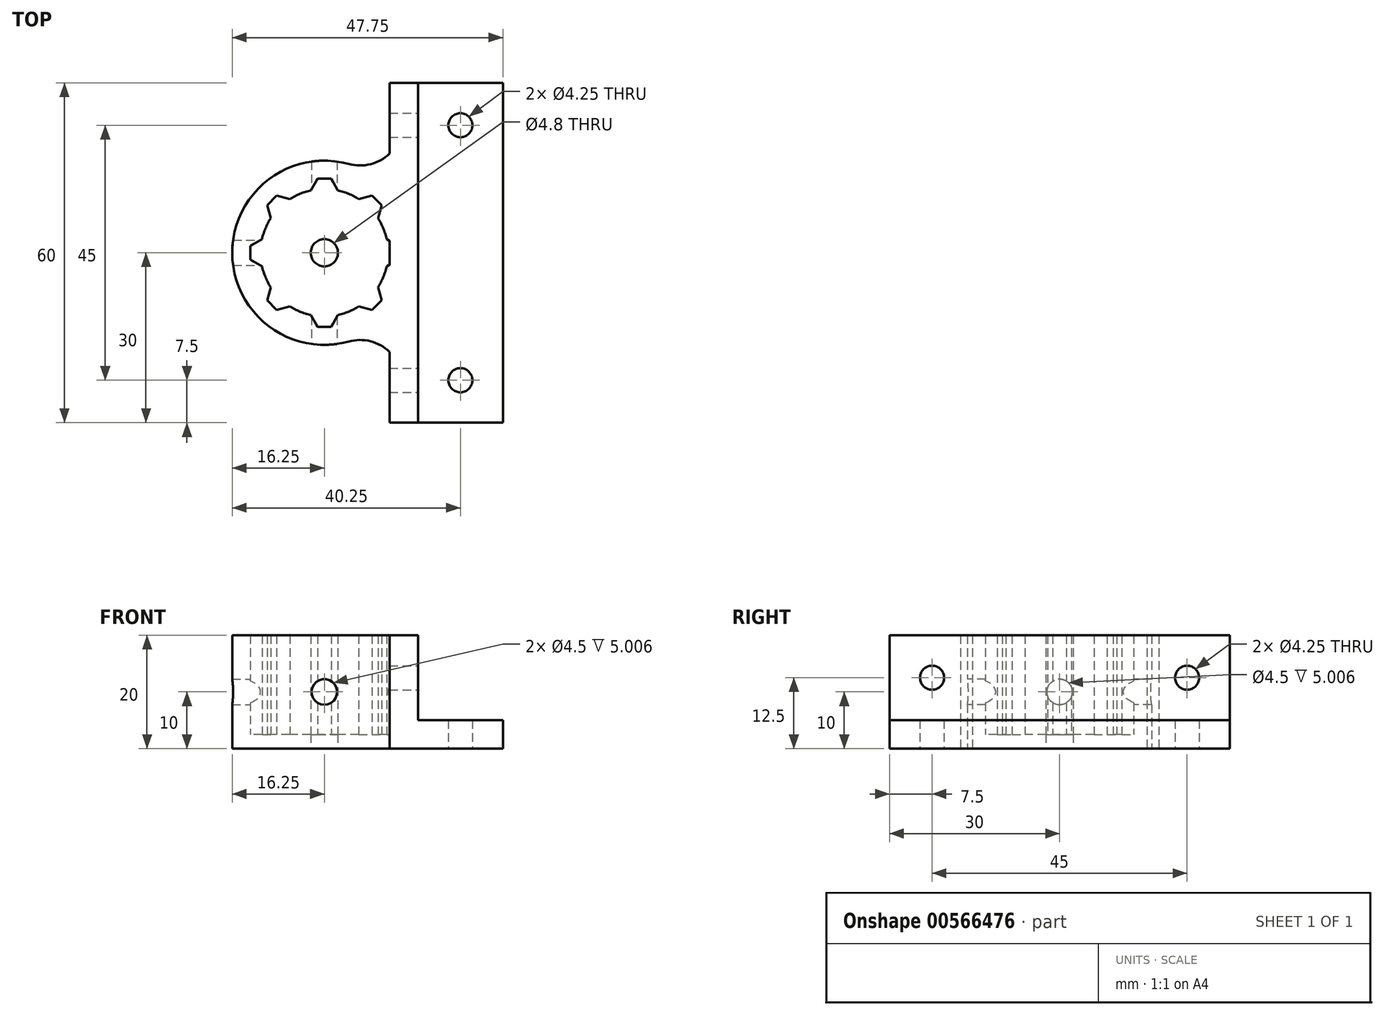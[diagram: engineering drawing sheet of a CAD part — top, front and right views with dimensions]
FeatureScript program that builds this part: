
annotation { "Feature Type Name" : "Feature", "Feature Type Description" : "" }
export const myFeature = defineFeature(function(context is Context, id is Id, definition is map)
    precondition{}
    {
        {
            var Q0;
            Q0=qCreatedBy(makeId("Top.planeOp"),FACE);
            var sketch = newSketch(context, id + "F0", { "sketchPlane" : qUnion([Q0])});
            skCircle(sketch, "E0", {"center": v(0, 0) * mm, "radius": 11 * mm, "construction": true});
            skLineSegment(sketch, "E1.bottom", {"start": v(7.5, -30) * mm, "end": v(-7.5, -30) * mm});
            skLineSegment(sketch, "E1.top", {"start": v(7.5, 30) * mm, "end": v(-7.5, 30) * mm});
            skLineSegment(sketch, "E1.left", {"start": v(7.5, -30) * mm, "end": v(7.5, 30) * mm});
            skLineSegment(sketch, "E1.right", {"start": v(-7.5, -30) * mm, "end": v(-7.5, 30) * mm});
            skCircle(sketch, "E2", {"center": v(0, 22.5) * mm, "radius": 2.12 * mm});
            skCircle(sketch, "E3.MirrorC", {"center": v(0, -22.5) * mm, "radius": 2.12 * mm});
            skSolve(sketch);
        }
        {
            var Q0;
            Q0=qSketchRegion(id+"F0",true);
            extrude(context, id + "F1", {"entities" : qUnion([Q0]), "depth" : 5 * mm});
        }
        {
            var Q0;
            Q0=makeQuery(id+"F1.opExtrude","SWEPT_FACE",FACE,{"disambiguationData":[OSD([sQuery(id+"F0.wireOp",EDGE,"E1.right")])]});
            var sketch = newSketch(context, id + "F2", { "sketchPlane" : qUnion([Q0])});
            skLineSegment(sketch, "E4.bottom", {"start": v(30, 0) * mm, "end": v(-30, 0) * mm});
            skLineSegment(sketch, "E4.top", {"start": v(30, 20) * mm, "end": v(-30, 20) * mm});
            skLineSegment(sketch, "E4.left", {"start": v(30, 0) * mm, "end": v(30, 20) * mm});
            skLineSegment(sketch, "E4.right", {"start": v(-30, 0) * mm, "end": v(-30, 20) * mm});
            skPoint(sketch, "E4.middle", {"position": v(0, 10) * mm});
            skCircle(sketch, "E5", {"center": v(-22.5, 12.5) * mm, "radius": 2.12 * mm});
            skCircle(sketch, "E6.MirrorC", {"center": v(22.5, 12.5) * mm, "radius": 2.12 * mm});
            skSolve(sketch);
        }
        {
            var Q0;
            Q0=qSketchRegion(id+"F2",true);
            extrude(context, id + "F3", {"entities" : qUnion([Q0]), "operationType" : NewBodyOperationType.ADD, "depth" : 5 * mm});
        }
        {
            var Q0;
            Q0=qCreatedBy(makeId("Top.planeOp"),FACE);
            var sketch = newSketch(context, id + "F4", { "sketchPlane" : qUnion([Q0])});
            skArc(sketch, "E7", {"start": v(-26.4, 11) * mm, "mid": v(-28.3, 10.4) * mm, "end": v(-30.07, 9.47) * mm});
            skArc(sketch, "E8", {"start": v(-19.7, 15.67) * mm, "mid": v(-40.25, 0) * mm, "end": v(-19.7, -15.67) * mm});
            skArc(sketch, "E9", {"start": v(-19.7, 15.67) * mm, "mid": v(-15.85, 15.63) * mm, "end": v(-12.5, 17.5) * mm});
            skArc(sketch, "E10.MirrorCS", {"start": v(-19.7, -15.67) * mm, "mid": v(-15.85, -15.63) * mm, "end": v(-12.5, -17.5) * mm});
            skLineSegment(sketch, "E11", {"start": v(-12.5, 17.5) * mm, "end": v(-12.5, 2.1) * mm});
            skCircle(sketch, "E12.cCircle", {"center": v(-13, 0) * mm, "radius": 2.08 * mm, "construction": true});
            skLineSegment(sketch, "E12.0", {"start": v(-10.93, 1.2) * mm, "end": v(-10.93, -1.2) * mm, "construction": true});
            skLineSegment(sketch, "E12.1", {"start": v(-12.5, -2.1) * mm, "end": v(-13, -2.4) * mm});
            skLineSegment(sketch, "E12.2", {"start": v(-13, -2.4) * mm, "end": v(-15.09, -1.2) * mm, "construction": true});
            skLineSegment(sketch, "E12.3", {"start": v(-15.09, -1.2) * mm, "end": v(-15.09, 1.2) * mm, "construction": true});
            skLineSegment(sketch, "E12.4", {"start": v(-15.09, 1.2) * mm, "end": v(-13, 2.4) * mm, "construction": true});
            skLineSegment(sketch, "E12.5", {"start": v(-13, 2.4) * mm, "end": v(-12.5, 2.1) * mm});
            skPoint(sketch, "E12.0.midPoint", {"position": v(-10.93, 0) * mm});
            skLineSegment(sketch, "E13.1.0", {"start": v(-17.93, 9.47) * mm, "end": v(-15.6, 10.1) * mm});
            skLineSegment(sketch, "E13.1.1", {"start": v(-15.6, 10.1) * mm, "end": v(-13.9, 8.4) * mm});
            skLineSegment(sketch, "E13.1.2", {"start": v(-13.9, 8.4) * mm, "end": v(-14.53, 6.07) * mm});
            skLineSegment(sketch, "E13.2.0", {"start": v(-26.4, 11) * mm, "end": v(-25.2, 13.07) * mm});
            skLineSegment(sketch, "E13.2.1", {"start": v(-25.2, 13.07) * mm, "end": v(-22.8, 13.07) * mm});
            skLineSegment(sketch, "E13.2.2", {"start": v(-22.8, 13.07) * mm, "end": v(-21.6, 11) * mm});
            skLineSegment(sketch, "E13.3.0", {"start": v(-33.47, 6.07) * mm, "end": v(-34.1, 8.4) * mm});
            skLineSegment(sketch, "E13.3.1", {"start": v(-34.1, 8.4) * mm, "end": v(-32.4, 10.1) * mm});
            skLineSegment(sketch, "E13.3.2", {"start": v(-32.4, 10.1) * mm, "end": v(-30.07, 9.47) * mm});
            skLineSegment(sketch, "E13.4.0", {"start": v(-35, -2.4) * mm, "end": v(-37.07, -1.2) * mm});
            skLineSegment(sketch, "E13.4.1", {"start": v(-37.07, -1.2) * mm, "end": v(-37.07, 1.2) * mm});
            skLineSegment(sketch, "E13.4.2", {"start": v(-37.07, 1.2) * mm, "end": v(-35, 2.4) * mm});
            skLineSegment(sketch, "E13.5.0", {"start": v(-30.07, -9.47) * mm, "end": v(-32.4, -10.1) * mm});
            skLineSegment(sketch, "E13.5.1", {"start": v(-32.4, -10.1) * mm, "end": v(-34.1, -8.4) * mm});
            skLineSegment(sketch, "E13.5.2", {"start": v(-34.1, -8.4) * mm, "end": v(-33.47, -6.07) * mm});
            skLineSegment(sketch, "E13.6.0", {"start": v(-21.6, -11) * mm, "end": v(-22.8, -13.07) * mm});
            skLineSegment(sketch, "E13.6.1", {"start": v(-22.8, -13.07) * mm, "end": v(-25.2, -13.07) * mm});
            skLineSegment(sketch, "E13.6.2", {"start": v(-25.2, -13.07) * mm, "end": v(-26.4, -11) * mm});
            skLineSegment(sketch, "E13.7.0", {"start": v(-14.53, -6.07) * mm, "end": v(-13.9, -8.4) * mm});
            skLineSegment(sketch, "E13.7.1", {"start": v(-13.9, -8.4) * mm, "end": v(-15.6, -10.1) * mm});
            skLineSegment(sketch, "E13.7.2", {"start": v(-15.6, -10.1) * mm, "end": v(-17.93, -9.47) * mm});
            skArc(sketch, "E14.trimOffspring", {"start": v(-17.93, 9.47) * mm, "mid": v(-19.7, 10.4) * mm, "end": v(-21.6, 11) * mm});
            skArc(sketch, "E15.trimOffspring", {"start": v(-33.47, 6.07) * mm, "mid": v(-34.4, 4.3) * mm, "end": v(-35, 2.4) * mm});
            skArc(sketch, "E16.trimOffspring", {"start": v(-35, -2.4) * mm, "mid": v(-34.4, -4.3) * mm, "end": v(-33.47, -6.07) * mm});
            skArc(sketch, "E17.trimOffspring", {"start": v(-30.07, -9.47) * mm, "mid": v(-28.3, -10.4) * mm, "end": v(-26.4, -11) * mm});
            skArc(sketch, "E18.trimOffspring", {"start": v(-21.6, -11) * mm, "mid": v(-19.7, -10.4) * mm, "end": v(-17.93, -9.47) * mm});
            skArc(sketch, "E19.trimOffspring", {"start": v(-14.53, -6.07) * mm, "mid": v(-13.6, -4.3) * mm, "end": v(-13, -2.4) * mm});
            skArc(sketch, "E20.trimOffspring", {"start": v(-13, 2.4) * mm, "mid": v(-13.6, 4.3) * mm, "end": v(-14.53, 6.07) * mm});
            skLineSegment(sketch, "E21.trimOffspring", {"start": v(-12.5, -2.1) * mm, "end": v(-12.5, -17.5) * mm});
            skSolve(sketch);
        }
        {
            var Q0;
            Q0=qSketchRegion(id+"F4",true);
            extrude(context, id + "F5", {"entities" : qUnion([Q0]), "operationType" : NewBodyOperationType.ADD, "depth" : 20 * mm});
        }
        {
            var Q0;
            Q0=qCreatedBy(makeId("Front.planeOp"),FACE);
            var sketch = newSketch(context, id + "F6", { "sketchPlane" : qUnion([Q0])});
            skCircle(sketch, "E22", {"center": v(-24, 10) * mm, "radius": 2.25 * mm});
            skSolve(sketch);
        }
        {
            var Q0;
            Q0=qSketchRegion(id+"F6",true);
            extrude(context, id + "F7", {"entities" : qUnion([Q0]), "operationType" : NewBodyOperationType.REMOVE, "endBound" : BoundingType.SYMMETRIC, "oppositeDirection" : true, "depth" : 35 * mm});
        }
        {
            var Q0;
            {var subQ30=sQuery(id+"F4.wireOp",EDGE,"E12.1");var subQ36=sQuery(id+"F2.wireOp",EDGE,"E4.bottom");var subQ37=sQuery(id+"F2.wireOp",EDGE,"E4.top");Q0=makeQuery(id+"F5.boolean.opBoolean","SPLIT",FACE,{"disambiguationData":[TD([makeQuery(id+"F5.opExtrude","SWEPT_FACE",FACE,{"disambiguationData":[OSD([subQ30])]})])],"derivedFrom":makeQuery(id+"F3.opExtrude","CAP_FACE",FACE,{"disambiguationData":[OSD([subQ36,subQ37,sQuery(id+"F2.wireOp",EDGE,"E4.left"),sQuery(id+"F2.wireOp",EDGE,"E4.right"),sQuery(id+"F2.wireOp",EDGE,"E5"),sQuery(id+"F2.wireOp",EDGE,"E6.MirrorC")])],"isStart":false})});}
            var sketch = newSketch(context, id + "F8", { "sketchPlane" : qUnion([Q0])});
            skCircle(sketch, "E23", {"center": v(0, 10) * mm, "radius": 2.25 * mm});
            skPoint(sketch, "E23.centerSnap0", {"position": v(-2.1, 10) * mm});
            skSolve(sketch);
        }
        {
            var Q0;
            Q0=qSketchRegion(id+"F8",true);
            extrude(context, id + "F9", {"entities" : qUnion([Q0]), "operationType" : NewBodyOperationType.REMOVE, "endBound" : BoundingType.THROUGH_ALL, "depth" : 25 * mm});
        }
        {
            var Q0;
            Q0=qCreatedBy(makeId("Top.planeOp"),FACE);
            var sketch = newSketch(context, id + "F10", { "sketchPlane" : qUnion([Q0])});
            skCircle(sketch, "E24", {"center": v(-24, 0) * mm, "radius": 2.4 * mm});
            skCircle(sketch, "E25", {"center": v(-24, 0) * mm, "radius": 13.12 * mm});
            skSolve(sketch);
        }
        {
            var Q0;
            Q0=qSketchRegion(id+"F10",true);
            extrude(context, id + "F11", {"entities" : qUnion([Q0]), "operationType" : NewBodyOperationType.ADD, "depth" : 2.5 * mm});
        }
    });
